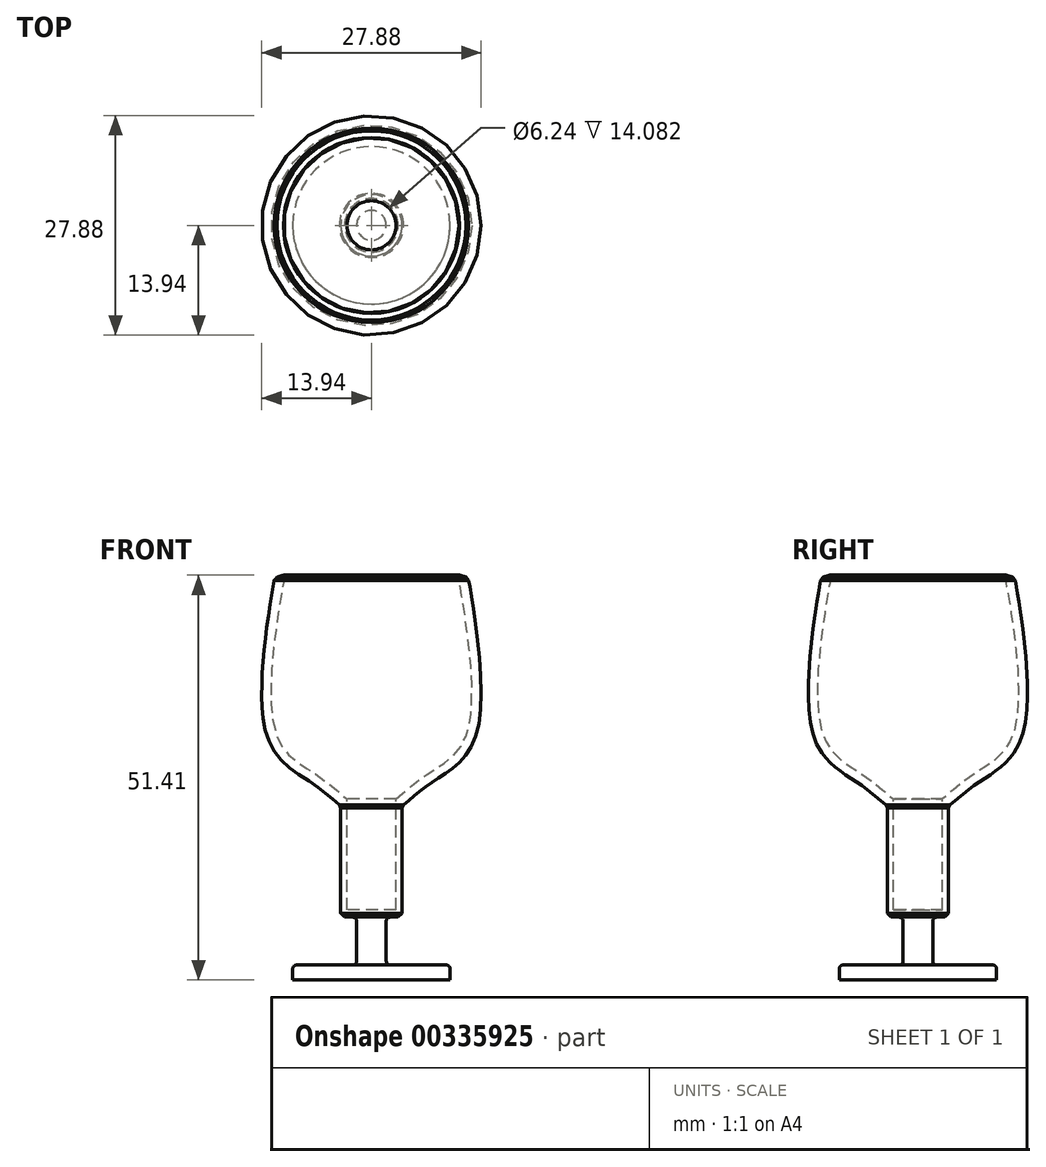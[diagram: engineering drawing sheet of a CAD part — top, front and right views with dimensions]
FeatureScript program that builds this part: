
annotation { "Feature Type Name" : "Feature", "Feature Type Description" : "" }
export const myFeature = defineFeature(function(context is Context, id is Id, definition is map)
    precondition{}
    {
        {
            var Q0;
            Q0=qCreatedBy(makeId("Front.planeOp"),FACE);
            var sketch = newSketch(context, id + "F0", { "sketchPlane" : qUnion([Q0])});
            skLineSegment(sketch, "E0", {"start": v(0, 0) * mm, "end": v(10, 0) * mm});
            skLineSegment(sketch, "E1", {"start": v(10, 0) * mm, "end": v(10, 1.89) * mm});
            skLineSegment(sketch, "E2", {"start": v(10, 1.89) * mm, "end": v(1.88, 1.89) * mm});
            skLineSegment(sketch, "E3", {"start": v(1.88, 1.89) * mm, "end": v(1.88, 7.97) * mm});
            skLineSegment(sketch, "E4", {"start": v(3.9, 7.97) * mm, "end": v(1.88, 7.97) * mm});
            skLineSegment(sketch, "E5", {"start": v(3.9, 7.97) * mm, "end": v(3.9, 22.06) * mm});
            skFitSpline(sketch, "E6", {"points": [v(3.9, 22.06) * mm, v(8.01, 25.3) * mm, v(13.55, 32.07) * mm, v(12.32, 50.98) * mm, v(12.32, 51.07) * mm], "startDerivative": vector(16.37, 14.11) * mm, "endDerivative": vector(0.36, 1.22) * mm});
            skFitSpline(sketch, "E7.0", {"points": [v(3.12, 22.97) * mm, v(3.46, 23.27) * mm, v(4.15, 23.86) * mm, v(5.06, 24.61) * mm, v(5.83, 25.22) * mm, v(6.44, 25.67) * mm, v(7.08, 26.12) * mm, v(7.76, 26.57) * mm, v(8.43, 27) * mm, v(9.3, 27.58) * mm, v(10.3, 28.38) * mm, v(11.17, 29.38) * mm, v(11.75, 30.39) * mm, v(12.11, 31.28) * mm, v(12.4, 32.33) * mm, v(12.6, 33.6) * mm, v(12.72, 35.04) * mm, v(12.76, 37.12) * mm, v(12.63, 39.94) * mm, v(12.35, 42.77) * mm, v(12.08, 44.88) * mm, v(11.86, 46.36) * mm, v(11.66, 47.7) * mm, v(11.5, 48.65) * mm, v(11.39, 49.3) * mm, v(11.31, 49.74) * mm, v(11.25, 50.1) * mm, v(11.2, 50.41) * mm, v(11.16, 50.61) * mm, v(11.14, 50.74) * mm, v(11.13, 50.83) * mm, v(11.12, 50.93) * mm, v(11.12, 51.04) * mm, v(11.12, 51.17) * mm, v(11.14, 51.28) * mm, v(11.16, 51.38) * mm, v(11.17, 51.4) * mm, v(11.17, 51.4) * mm]});
            skLineSegment(sketch, "E8", {"start": v(3.12, 22.97) * mm, "end": v(3.12, 8.9) * mm});
            skLineSegment(sketch, "E9", {"start": v(3.12, 8.9) * mm, "end": v(1.42, 8.9) * mm});
            skLineSegment(sketch, "E10", {"start": v(1.42, 8.9) * mm, "end": v(0, 8.9) * mm});
            skLineSegment(sketch, "E11", {"start": v(0, 8.9) * mm, "end": v(0, 0) * mm});
            skLineSegment(sketch, "E12", {"start": v(11.17, 51.4) * mm, "end": v(12.32, 51.07) * mm});
            skSolve(sketch);
        }
        {
            var Q0;
            Q0=makeQuery(id+"F0.imprint","IMPRINT",FACE,{"disambiguationData":[TD([[makeQuery(id+"F0.imprint","IMPRINT",EDGE,{"derivedFrom":sQuery(id+"F0.wireOp",EDGE,"E0")}),1.0]])]});
            var Q1;
            Q1=sQuery(id+"F0.wireOp",EDGE,"E11");
            revolve(context, id + "F1", {"entities" : qUnion([Q0]), "axis" : qUnion([Q1]), "revolveType" : RevolveType.FULL});
        }
        {
            var Q0;
            Q0=makeQuery(id+"F1.opRevolve","SWEPT_FACE",FACE,{"disambiguationData":[OSD([sQuery(id+"F0.wireOp",EDGE,"E3")])]});
            var Q1;
            Q1=makeQuery(id+"F1.opRevolve","SWEPT_EDGE",EDGE,{"disambiguationData":[OSD([sQuery(id+"F0.wireOp",EDGE,"E1"),sQuery(id+"F0.wireOp",EDGE,"E2")])]});
            fillet(context, id + "F2", {"entities" : qUnion([Q0, Q1]), "radius" : 0.5 * mm, "tangentPropagation" : true, "allowEdgeOverflow" : false});
        }
        {
            var Q0;
            Q0=makeQuery(id+"F1.opRevolve","SWEPT_FACE",FACE,{"disambiguationData":[OSD([sQuery(id+"F0.wireOp",EDGE,"E6")])]});
            var Q1;
            Q1=makeQuery(id+"F1.opRevolve","SWEPT_EDGE",EDGE,{"disambiguationData":[OSD([sQuery(id+"F0.wireOp",EDGE,"E5"),sQuery(id+"F0.wireOp",EDGE,"E6")])]});
            var Q2;
            Q2=makeQuery(id+"F1.opRevolve","SWEPT_EDGE",EDGE,{"disambiguationData":[OSD([sQuery(id+"F0.wireOp",EDGE,"E4"),sQuery(id+"F0.wireOp",EDGE,"E5")])]});
            chamfer(context, id + "F3", {"entities" : qUnion([Q0, Q1, Q2]), "width" : 0.5 * mm, "tangentPropagation" : true});
        }
    });
